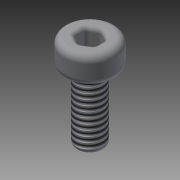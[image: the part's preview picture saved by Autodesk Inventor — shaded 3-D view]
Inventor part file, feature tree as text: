
AUTODESK INVENTOR PART (.ipt)
format: ipt  version: 2013 (Build 170138000, 138)  size: 177,664 bytes
history: native  units: mm
features: extrude x3, sketch x3, fillet x2, other x1, thread x1
ambient origin geometry x1: Origin
feature tree (10):
  other  "ソリッド1"
  extrude  "押し出し1"  Depth=3.8mm
  extrude  "押し出し2"  Depth=2.0mm TaperAngle=0.0deg
  extrude  "押し出し3"  Depth=2.0mm
  fillet  "フィレット1"  Radius=5.0mm
  fillet  "フィレット2"  Radius=0.75mm
  thread  "ねじ3"
  sketch  "スケッチ1"
  sketch  "スケッチ2"
  sketch  "スケッチ3"
